# Revit family: ROTHOB_Rothoblaas_Plate_Slot
name_source: partatom
category: Structural Connections
units: mm (PartAtom-declared; Revit-internal decimal feet)

## family parameters
Cut with Voids When Loaded = No
Enable cutting in views = Yes
Host = Face
Material for Model Behavior = Other
OmniClass Number = 23.13.23.11.19.13
OmniClass Title = Wood Connectors
Shared = No

## types (1)
- SLOT90_89x40x120mm
    BIMObjectName = ROTHOB_Rothoblaas_Plate_Slot
    CECode = ETA-19/0167
    Category = Pr_20_76_51_07: Aluminium structural sections
    CodePerformance = CE - Construction products
    Color = Silver
    Default Elevation = 1219.2 mm  [stored 4 ft]
    Description = Connector for structural panels
    DurationUnit = Years
    Esporta tipo in formato IFC con nome = IfcMemberType
    ExpectedLife = 50
    Features = SLOT connector for edge connections for CLT, LVL and Glulam members
    Height_H = 40 mm  [stored 0.131234 ft]
    Hwedge = 34 mm
    IfcExportAs = IfcMemberType
    IfcExportType = USERDEFINED
    Length_L = 120 mm  [stored 0.393701 ft]
    ManufacturerName = ROTHO BLAAS SRL
    ManufacturerURL = www.rothoblaas.com
    Material = Aluminium
    MinWeight = 0.4 kg
    ModelDisclaimer = The latest version of the data sheets can be found on our website
    ModelNumber = SLOT90
    Name = Plate
    NominalHeight = 40 mm  [stored 0.131234 ft]
    NominalLength = 120 mm  [stored 0.393701 ft]
    NominalWidth = 89 mm  [stored 0.291995 ft]
    ObjectMaterial = ROTHOB_Rothoblaas_Aluminium
    OmniClassCode = 23-13 23 11 19 13
    OmniClassTitle = Wood Connectors
    OmniClassVersion = 2012-05-16
    ProductInformation = https://www.rothoblaas.com
    Revision = 1
    ScrewNumber_nscrews = 2
    Shape = Three-dimensional
    Size = 89x40x120 mm
    Tipo IFC predefinito = USERDEFINED
    UniClass2015Code = Pr_20_76_51_07
    UniClass2015Title = Aluminium structural sections
    UniClass2015Version = Products v1.33
    Version = 2
    Width_B = 89 mm  [stored 0.291995 ft]

note: [stored X ft] marks values corroborated as IEEE doubles in the binary element streams (Revit-internal decimal feet)
